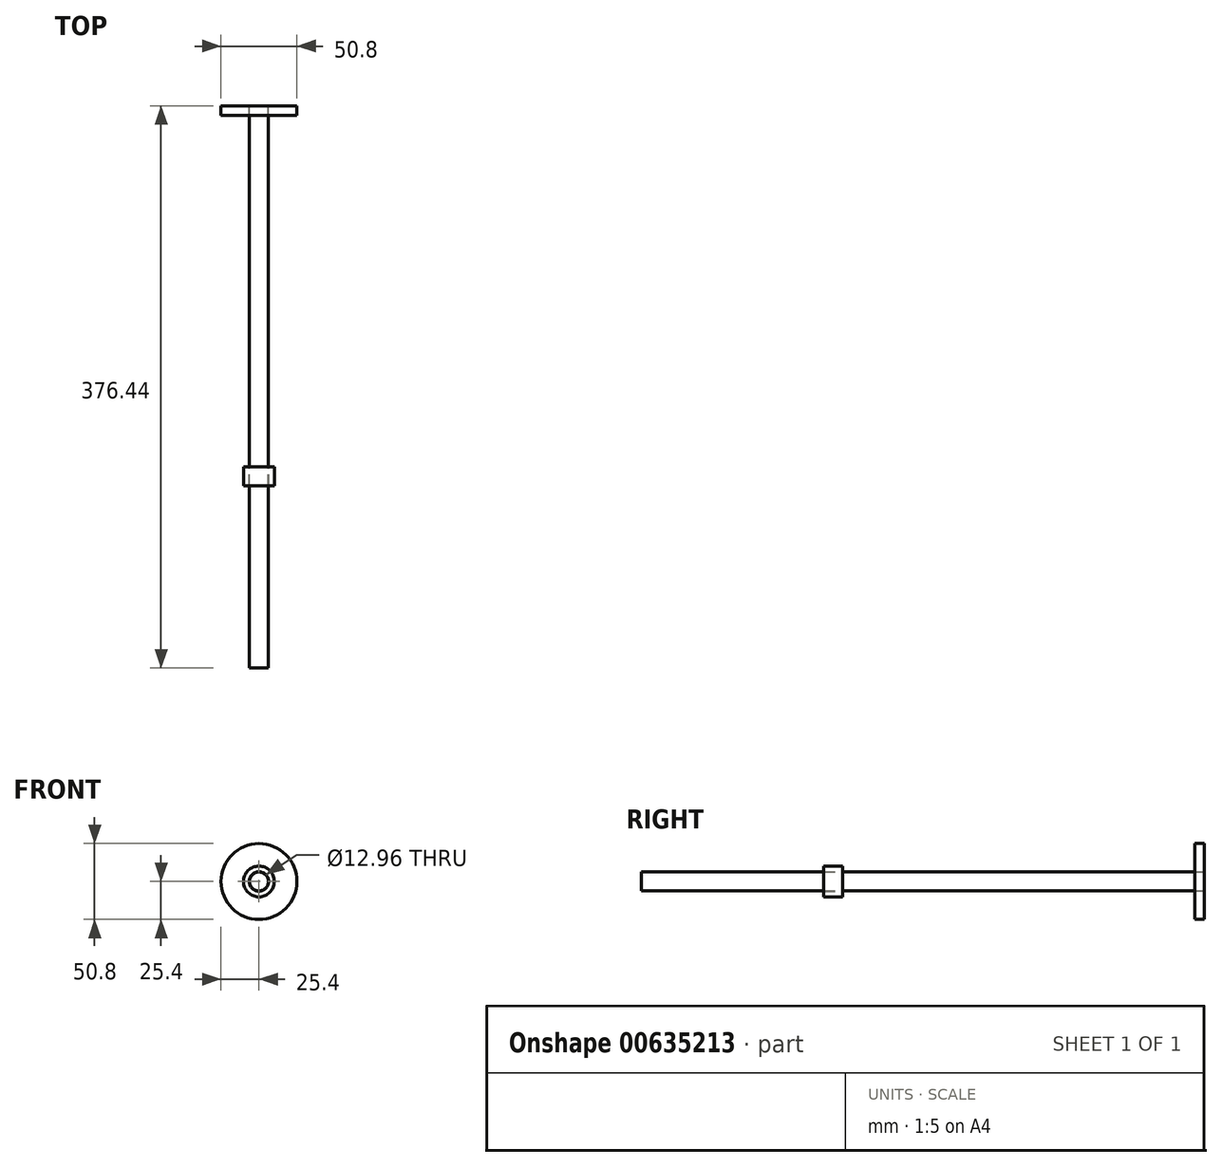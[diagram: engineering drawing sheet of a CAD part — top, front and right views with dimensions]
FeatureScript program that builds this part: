
annotation { "Feature Type Name" : "Feature", "Feature Type Description" : "" }
export const myFeature = defineFeature(function(context is Context, id is Id, definition is map)
    precondition{}
    {
        {
            var Q0;
            Q0=qCreatedBy(makeId("Right.planeOp"),FACE);
            var sketch = newSketch(context, id + "F0", { "sketchPlane" : qUnion([Q0])});
            skLineSegment(sketch, "E0", {"start": v(0, 0) * mm, "end": v(-304.8, 0) * mm});
            skLineSegment(sketch, "E1", {"start": v(0, 0) * mm, "end": v(0, -6.35) * mm});
            skLineSegment(sketch, "E2", {"start": v(0, -6.35) * mm, "end": v(-304.8, -6.35) * mm});
            skLineSegment(sketch, "E3", {"start": v(-305.24, 47.34) * mm, "end": v(-305.03, 40.03) * mm});
            skPoint(sketch, "E4.7.internal.snap0", {"position": v(-305.14, 43.69) * mm});
            skLineSegment(sketch, "E5", {"start": v(-304.8, 2.92) * mm, "end": v(-310.03, 2.92) * mm});
            skLineSegment(sketch, "E6", {"start": v(-310.03, 2.92) * mm, "end": v(-315.37, 5.82) * mm});
            skLineSegment(sketch, "E7", {"start": v(-315.37, 5.82) * mm, "end": v(-319.39, 10.5) * mm});
            skLineSegment(sketch, "E8", {"start": v(-304.8, -6.35) * mm, "end": v(-376.44, -6.35) * mm});
            skLineSegment(sketch, "E9", {"start": v(-376.44, -6.35) * mm, "end": v(-376.44, 0) * mm});
            skLineSegment(sketch, "E10", {"start": v(-376.44, 0) * mm, "end": v(-304.8, 0) * mm});
            skSolve(sketch);
        }
        {
            var Q0;
            Q0=makeQuery(id+"F0.imprint","IMPRINT",FACE,{"disambiguationData":[TD([[makeQuery(id+"F0.imprint","IMPRINT",EDGE,{"derivedFrom":sQuery(id+"F0.wireOp",EDGE,"E0")}),1.0]])]});
            var Q1;
            Q1=sQuery(id+"F0.wireOp",EDGE,"E0");
            revolve(context, id + "F1", {"entities" : qUnion([Q0]), "axis" : qUnion([Q1]), "revolveType" : RevolveType.FULL});
        }
        {
            var Q0;
            Q0=qCreatedBy(makeId("Front.planeOp"),FACE);
            var sketch = newSketch(context, id + "F2", { "sketchPlane" : qUnion([Q0])});
            skCircle(sketch, "E11", {"center": v(0, 0) * mm, "radius": 25.4 * mm});
            skSolve(sketch);
        }
        {
            var Q0;
            Q0=makeQuery(id+"F2.imprint","IMPRINT",FACE,{"disambiguationData":[TD([[makeQuery(id+"F2.imprint","IMPRINT",EDGE,{"derivedFrom":sQuery(id+"F2.wireOp",EDGE,"E11")}),1.0]])]});
            var Q1;
            Q1 = qConstructionFilter(qBodyType(qCreatedBy(id + "F2" ,EDGE), BodyType.WIRE), ConstructionObject.NO);
            extrude(context, id + "F3", {"entities" : qUnion([Q0]), "surfaceEntities" : qUnion([Q1]), "depth" : 6.35 * mm, "offsetDistance" : 25.4 * mm});
        }
        {
            var Q0;
            Q0=qCreatedBy(makeId("Right.planeOp"),FACE);
            var sketch = newSketch(context, id + "F4", { "sketchPlane" : qUnion([Q0])});
            skLineSegment(sketch, "E12", {"start": v(-254.4, 6.48) * mm, "end": v(-254.4, 10.3) * mm});
            skLineSegment(sketch, "E13", {"start": v(-254.4, 10.3) * mm, "end": v(-241.7, 10.3) * mm});
            skLineSegment(sketch, "E14", {"start": v(-241.7, 10.3) * mm, "end": v(-241.7, 6.48) * mm});
            skLineSegment(sketch, "E15", {"start": v(-241.7, 6.48) * mm, "end": v(-254.4, 6.48) * mm});
            skSolve(sketch);
        }
        {
            var Q0;
            Q0=makeQuery(id+"F4.imprint","IMPRINT",FACE,{"disambiguationData":[TD([[makeQuery(id+"F4.imprint","IMPRINT",EDGE,{"derivedFrom":sQuery(id+"F4.wireOp",EDGE,"E12")}),-1.0]])]});
            var Q1;
            Q1=sQuery(id+"F0.wireOp",EDGE,"E0");
            revolve(context, id + "F5", {"entities" : qUnion([Q0]), "axis" : qUnion([Q1]), "revolveType" : RevolveType.FULL});
        }
    });
